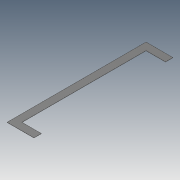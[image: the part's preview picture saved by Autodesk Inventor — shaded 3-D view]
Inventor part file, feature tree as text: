
AUTODESK INVENTOR PART (.ipt)
format: ipt  version: 2020 (Build 240168000, 168)  size: 96,768 bytes
history: native  units: mm
features: extrude x2, sketch x2, other x1
ambient origin geometry x8: Origin, YZ Plane, XZ Plane, XY Plane, X Axis, Y Axis, Z Axis, Center Point
bodies: Body1 (feature_tree)
feature tree (5):
  other  "ソリッド1"
  extrude  "押し出し1"  Depth=1500.0mm
  extrude  "押し出し2"  Depth=290.0mm
  sketch  "スケッチ1"
  sketch  "スケッチ2"
